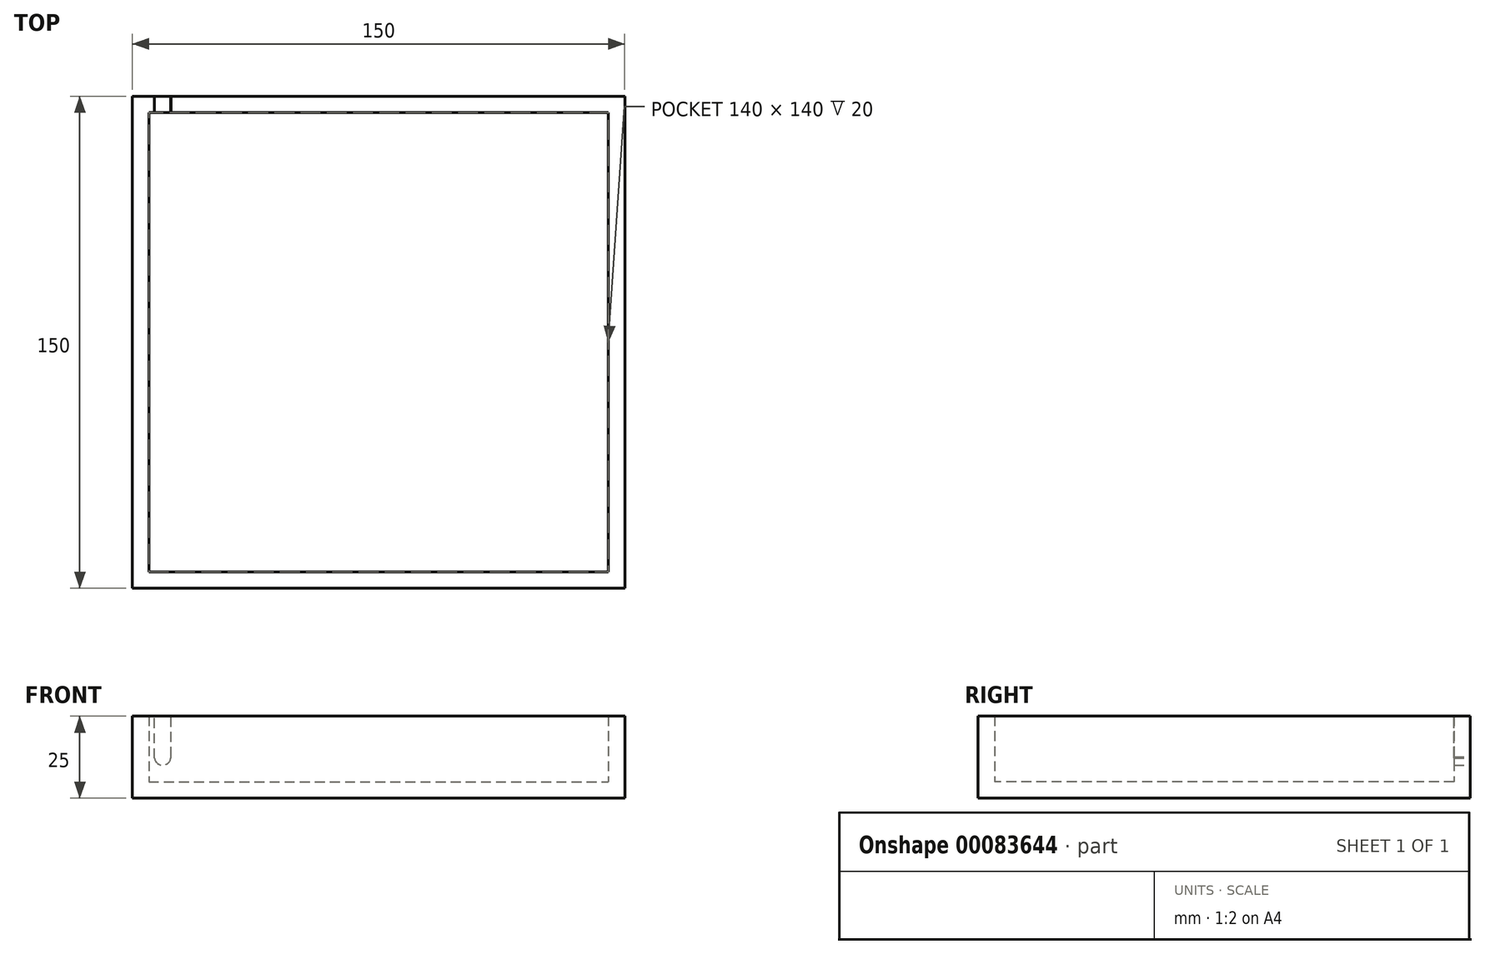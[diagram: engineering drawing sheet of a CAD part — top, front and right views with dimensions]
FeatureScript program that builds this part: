
annotation { "Feature Type Name" : "Feature", "Feature Type Description" : "" }
export const myFeature = defineFeature(function(context is Context, id is Id, definition is map)
    precondition{}
    {
        {
            var Q0;
            Q0=qCreatedBy(makeId("Top.planeOp"),FACE);
            var sketch = newSketch(context, id + "F0", { "sketchPlane" : qUnion([Q0])});
            skLineSegment(sketch, "E0.bottom", {"start": v(-65.89, 72.73) * mm, "end": v(84.11, 72.73) * mm});
            skLineSegment(sketch, "E0.top", {"start": v(-65.89, -77.27) * mm, "end": v(84.11, -77.27) * mm});
            skLineSegment(sketch, "E0.left", {"start": v(-65.89, 72.73) * mm, "end": v(-65.89, -77.27) * mm});
            skLineSegment(sketch, "E0.right", {"start": v(84.11, 72.73) * mm, "end": v(84.11, -77.27) * mm});
            skLineSegment(sketch, "E1.bottom", {"start": v(-60.89, 67.73) * mm, "end": v(79.11, 67.73) * mm});
            skLineSegment(sketch, "E1.top", {"start": v(-60.89, -72.27) * mm, "end": v(79.11, -72.27) * mm});
            skLineSegment(sketch, "E1.left", {"start": v(-60.89, 67.73) * mm, "end": v(-60.89, -72.27) * mm});
            skLineSegment(sketch, "E1.right", {"start": v(79.11, 67.73) * mm, "end": v(79.11, -72.27) * mm});
            skSolve(sketch);
        }
        {
            var Q0;
            Q0=makeQuery(id+"F0.imprint","IMPRINT",FACE,{"disambiguationData":[TD([[makeQuery(id+"F0.imprint","IMPRINT",EDGE,{"derivedFrom":sQuery(id+"F0.wireOp",EDGE,"E0.bottom")}),-1.0]])]});
            extrude(context, id + "F1", {"entities" : qUnion([Q0]), "depth" : 25 * mm});
        }
        {
            var Q0;
            Q0=makeQuery(id+"F0.imprint","IMPRINT",FACE,{"disambiguationData":[TD([[makeQuery(id+"F0.imprint","IMPRINT",EDGE,{"derivedFrom":sQuery(id+"F0.wireOp",EDGE,"E1.bottom")}),-1.0]])]});
            extrude(context, id + "F2", {"entities" : qUnion([Q0]), "operationType" : NewBodyOperationType.ADD, "depth" : 5 * mm});
        }
        {
            var Q0;
            Q0=makeQuery(id+"F1.opExtrude","SWEPT_FACE",FACE,{"disambiguationData":[OSD([sQuery(id+"F0.wireOp",EDGE,"E0.bottom")])]});
            var sketch = newSketch(context, id + "F3", { "sketchPlane" : qUnion([Q0])});
            skCircle(sketch, "E2", {"center": v(56.68, 12.5) * mm, "radius": 2.5 * mm});
            skSolve(sketch);
        }
        {
            var Q0;
            Q0 = qSketchRegion(id + "F3", true);
            extrude(context, id + "F4", {"entities" : qUnion([Q0]), "operationType" : NewBodyOperationType.REMOVE, "oppositeDirection" : true, "depth" : 6 * mm});
        }
        {
            var Q0;
            Q0=makeQuery(id+"F1.opExtrude","CAP_FACE",FACE,{"disambiguationData":[OSD([sQuery(id+"F0.wireOp",EDGE,"E0.bottom"),sQuery(id+"F0.wireOp",EDGE,"E0.top"),sQuery(id+"F0.wireOp",EDGE,"E0.left"),sQuery(id+"F0.wireOp",EDGE,"E0.right"),sQuery(id+"F0.wireOp",EDGE,"E1.bottom"),sQuery(id+"F0.wireOp",EDGE,"E1.top"),sQuery(id+"F0.wireOp",EDGE,"E1.left"),sQuery(id+"F0.wireOp",EDGE,"E1.right")])],"isStart":false});
            var sketch = newSketch(context, id + "F5", { "sketchPlane" : qUnion([Q0])});
            skLineSegment(sketch, "E3.bottom", {"start": v(-59.19, 67.73) * mm, "end": v(-54.19, 67.73) * mm});
            skLineSegment(sketch, "E3.top", {"start": v(-59.19, 72.73) * mm, "end": v(-54.19, 72.73) * mm});
            skLineSegment(sketch, "E3.left", {"start": v(-59.19, 67.73) * mm, "end": v(-59.19, 72.73) * mm});
            skLineSegment(sketch, "E3.right", {"start": v(-54.19, 67.73) * mm, "end": v(-54.19, 72.73) * mm});
            skSolve(sketch);
        }
        {
            var Q0;
            Q0 = qSketchRegion(id + "F5", true);
            extrude(context, id + "F6", {"entities" : qUnion([Q0]), "operationType" : NewBodyOperationType.REMOVE, "oppositeDirection" : true, "depth" : 12.85 * mm});
        }
    });
